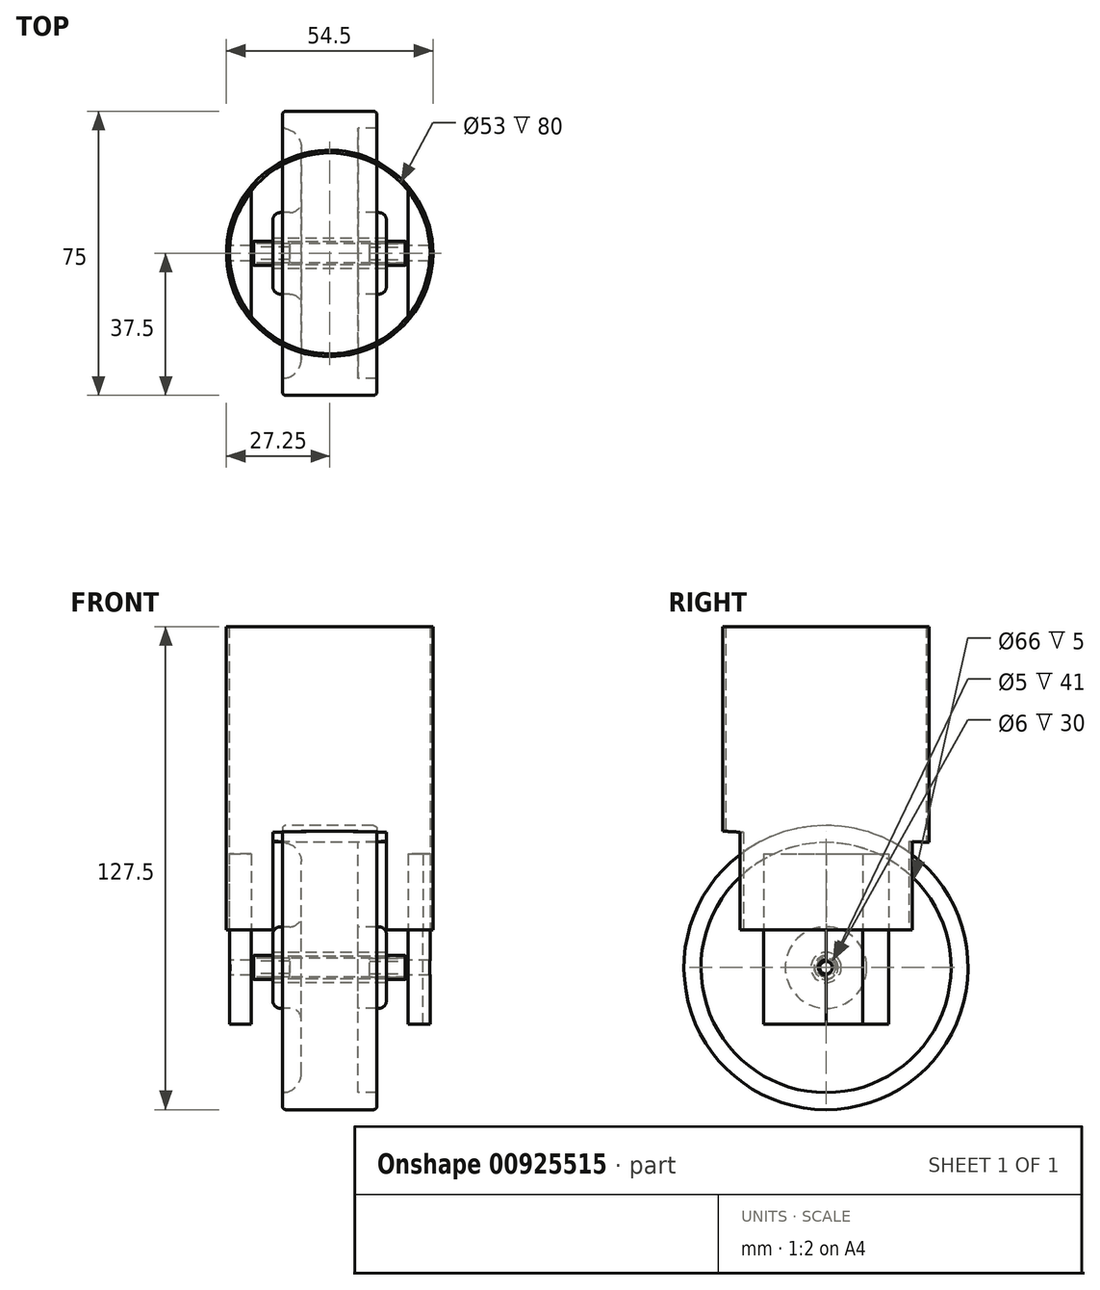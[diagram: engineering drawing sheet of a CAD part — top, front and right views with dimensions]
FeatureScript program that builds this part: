
annotation { "Feature Type Name" : "Feature", "Feature Type Description" : "" }
export const myFeature = defineFeature(function(context is Context, id is Id, definition is map)
    precondition{}
    {
        {
            var Q0;
            Q0=qCreatedBy(makeId("Right.planeOp"),FACE);
            var sketch = newSketch(context, id + "F0", { "sketchPlane" : qUnion([Q0])});
            skCircle(sketch, "E0", {"center": v(0, 0) * mm, "radius": 4 * mm});
            skCircle(sketch, "E1", {"center": v(0, 0) * mm, "radius": 10.75 * mm});
            skCircle(sketch, "E2", {"center": v(0, 0) * mm, "radius": 37.5 * mm});
            skCircle(sketch, "E3", {"center": v(0, 0) * mm, "radius": 33 * mm});
            skSolve(sketch);
        }
        {
            var Q0;
            Q0=makeQuery(id+"F0.imprint","IMPRINT",FACE,{"disambiguationData":[TD([[makeQuery(id+"F0.imprint","IMPRINT",EDGE,{"derivedFrom":sQuery(id+"F0.wireOp",EDGE,"E2")}),1.0]])]});
            extrude(context, id + "F1", {"entities" : qUnion([Q0]), "endBound" : BoundingType.SYMMETRIC, "depth" : 25 * mm, "offsetDistance" : 25 * mm});
        }
        {
            var Q0;
            Q0=makeQuery(id+"F0.imprint","IMPRINT",FACE,{"disambiguationData":[TD([[makeQuery(id+"F0.imprint","IMPRINT",EDGE,{"derivedFrom":sQuery(id+"F0.wireOp",EDGE,"E1")}),-1.0]])]});
            extrude(context, id + "F2", {"entities" : qUnion([Q0]), "operationType" : NewBodyOperationType.ADD, "endBound" : BoundingType.SYMMETRIC, "depth" : 15 * mm, "offsetDistance" : 25 * mm});
        }
        {
            var Q0;
            Q0=makeQuery(id+"F0.imprint","IMPRINT",FACE,{"disambiguationData":[TD([[makeQuery(id+"F0.imprint","IMPRINT",EDGE,{"derivedFrom":sQuery(id+"F0.wireOp",EDGE,"E0")}),-1.0]])]});
            extrude(context, id + "F3", {"entities" : qUnion([Q0]), "operationType" : NewBodyOperationType.ADD, "endBound" : BoundingType.SYMMETRIC, "depth" : 30 * mm, "offsetDistance" : 25 * mm});
        }
        {
            var Q0;
            Q0=makeQuery(id+"F2.opExtrude","CAP_EDGE",EDGE,{"disambiguationData":[OSD([sQuery(id+"F0.wireOp",EDGE,"E3")])],"isStart":false});
            var Q1;
            Q1=makeQuery(id+"F2.opExtrude","CAP_EDGE",EDGE,{"disambiguationData":[OSD([sQuery(id+"F0.wireOp",EDGE,"E3")])],"isStart":true});
            fillet(context, id + "F4", {"entities" : qUnion([Q0, Q1]), "radius" : 5 * mm, "tangentPropagation" : true, "allowEdgeOverflow" : false});
        }
        {
            var Q0;
            Q0=makeQuery(id+"F2.opExtrude","CAP_EDGE",EDGE,{"disambiguationData":[OSD([sQuery(id+"F0.wireOp",EDGE,"E1")])],"isStart":true});
            var Q1;
            Q1=makeQuery(id+"F2.opExtrude","CAP_EDGE",EDGE,{"disambiguationData":[OSD([sQuery(id+"F0.wireOp",EDGE,"E1")])],"isStart":false});
            fillet(context, id + "F5", {"entities" : qUnion([Q0, Q1]), "radius" : 3 * mm, "tangentPropagation" : true, "allowEdgeOverflow" : false});
        }
        {
            var Q0;
            Q0=makeQuery(id+"F3.opExtrude","CAP_EDGE",EDGE,{"disambiguationData":[OSD([sQuery(id+"F0.wireOp",EDGE,"E1")])],"isStart":false});
            var Q1;
            Q1=makeQuery(id+"F3.opExtrude","CAP_EDGE",EDGE,{"disambiguationData":[OSD([sQuery(id+"F0.wireOp",EDGE,"E1")])],"isStart":true});
            fillet(context, id + "F6", {"entities" : qUnion([Q0, Q1]), "radius" : 2 * mm, "tangentPropagation" : true, "allowEdgeOverflow" : false});
        }
        {
            var Q0;
            Q0=makeQuery(id+"F1.opExtrude","CAP_EDGE",EDGE,{"disambiguationData":[OSD([sQuery(id+"F0.wireOp",EDGE,"E2")])],"isStart":true});
            var Q1;
            {var subQ0=sQuery(id+"F0.wireOp",EDGE,"E3");Q1=makeQuery(id+"F4.opFillet","BLEND_EDGE",EDGE,{"blendedFrom":[makeQuery(id+"F2.opExtrude","CAP_EDGE",EDGE,{"disambiguationData":[OSD([subQ0])],"isStart":true}),makeQuery(id+"F1.opExtrude","CAP_FACE",FACE,{"disambiguationData":[OSD([sQuery(id+"F0.wireOp",EDGE,"E2"),subQ0])],"isStart":true})],"blendedInto":[makeQuery(id+"F1.opExtrude","CAP_FACE",FACE,{"disambiguationData":[OSD([sQuery(id+"F0.wireOp",EDGE,"E2"),subQ0])],"isStart":true})]});}
            var Q2;
            Q2=makeQuery(id+"F1.opExtrude","CAP_EDGE",EDGE,{"disambiguationData":[OSD([sQuery(id+"F0.wireOp",EDGE,"E2")])],"isStart":false});
            var Q3;
            {var subQ0=sQuery(id+"F0.wireOp",EDGE,"E3");Q3=makeQuery(id+"F4.opFillet","BLEND_EDGE",EDGE,{"blendedFrom":[makeQuery(id+"F2.opExtrude","CAP_EDGE",EDGE,{"disambiguationData":[OSD([subQ0])],"isStart":false}),makeQuery(id+"F1.opExtrude","CAP_FACE",FACE,{"disambiguationData":[OSD([sQuery(id+"F0.wireOp",EDGE,"E2"),subQ0])],"isStart":false})],"blendedInto":[makeQuery(id+"F1.opExtrude","CAP_FACE",FACE,{"disambiguationData":[OSD([sQuery(id+"F0.wireOp",EDGE,"E2"),subQ0])],"isStart":false})]});}
            fillet(context, id + "F7", {"entities" : qUnion([Q0, Q1, Q2, Q3]), "radius" : 1 * mm, "tangentPropagation" : true, "allowEdgeOverflow" : false});
        }
        {
            var Q0;
            Q0=qCreatedBy(makeId("Right.planeOp"),FACE);
            var sketch = newSketch(context, id + "F8", { "sketchPlane" : qUnion([Q0])});
            skCircle(sketch, "E4", {"center": v(0, 0) * mm, "radius": 4 * mm});
            skCircle(sketch, "E5", {"center": v(0, 0) * mm, "radius": 3 * mm});
            skSolve(sketch);
        }
        {
            var Q0;
            Q0=makeQuery(id+"F8.imprint","IMPRINT",FACE,{"disambiguationData":[TD([[makeQuery(id+"F8.imprint","IMPRINT",EDGE,{"derivedFrom":sQuery(id+"F8.wireOp",EDGE,"E4")}),1.0]])]});
            extrude(context, id + "F9", {"entities" : qUnion([Q0]), "endBound" : BoundingType.SYMMETRIC, "depth" : 30 * mm, "offsetDistance" : 25 * mm});
        }
        {
            var Q0;
            Q0=qCreatedBy(makeId("Right.planeOp"),FACE);
            var sketch = newSketch(context, id + "F10", { "sketchPlane" : qUnion([Q0])});
            skCircle(sketch, "E6", {"center": v(0, 0) * mm, "radius": 3 * mm});
            skCircle(sketch, "E7", {"center": v(0, 0) * mm, "radius": 2.5 * mm});
            skSolve(sketch);
        }
        {
            var Q0;
            Q0=makeQuery(id+"F10.imprint","IMPRINT",FACE,{"disambiguationData":[TD([[makeQuery(id+"F10.imprint","IMPRINT",EDGE,{"derivedFrom":sQuery(id+"F10.wireOp",EDGE,"E6")}),1.0]])]});
            extrude(context, id + "F11", {"entities" : qUnion([Q0]), "endBound" : BoundingType.SYMMETRIC, "depth" : 41 * mm, "offsetDistance" : 25 * mm});
        }
        {
            var Q0;
            Q0=makeQuery(id+"F11.opExtrude","CAP_FACE",FACE,{"disambiguationData":[OSD([sQuery(id+"F10.wireOp",EDGE,"E6"),sQuery(id+"F10.wireOp",EDGE,"E7")])],"isStart":false});
            var sketch = newSketch(context, id + "F12", { "sketchPlane" : qUnion([Q0])});
            skCircle(sketch, "E8", {"center": v(0, 0) * mm, "radius": 2.5 * mm});
            skCircle(sketch, "E9", {"center": v(0, 0) * mm, "radius": 1.65 * mm});
            skSolve(sketch);
        }
        {
            var Q0;
            Q0=makeQuery(id+"F12.imprint","IMPRINT",FACE,{"disambiguationData":[TD([[makeQuery(id+"F12.imprint","IMPRINT",EDGE,{"derivedFrom":sQuery(id+"F12.wireOp",EDGE,"E8")}),1.0]])]});
            extrude(context, id + "F13", {"entities" : qUnion([Q0]), "oppositeDirection" : true, "depth" : 10 * mm, "offsetDistance" : 25 * mm});
        }
        {
            var Q0;
            Q0=makeQuery(id+"F11.opExtrude","CAP_FACE",FACE,{"disambiguationData":[OSD([sQuery(id+"F10.wireOp",EDGE,"E6"),sQuery(id+"F10.wireOp",EDGE,"E7")])],"isStart":true});
            var sketch = newSketch(context, id + "F14", { "sketchPlane" : qUnion([Q0])});
            skCircle(sketch, "E10", {"center": v(0, 0) * mm, "radius": 2.5 * mm});
            skCircle(sketch, "E11", {"center": v(0, 0) * mm, "radius": 1.65 * mm});
            skSolve(sketch);
        }
        {
            var Q0;
            Q0=makeQuery(id+"F14.imprint","IMPRINT",FACE,{"disambiguationData":[TD([[makeQuery(id+"F14.imprint","IMPRINT",EDGE,{"derivedFrom":sQuery(id+"F14.wireOp",EDGE,"E10")}),-1.0]])]});
            extrude(context, id + "F15", {"entities" : qUnion([Q0]), "oppositeDirection" : true, "depth" : 10 * mm, "offsetDistance" : 25 * mm});
        }
        {
            var Q0;
            Q0=makeQuery(id+"F9.opExtrude","CAP_FACE",FACE,{"disambiguationData":[OSD([sQuery(id+"F8.wireOp",EDGE,"E4"),sQuery(id+"F8.wireOp",EDGE,"E5")])],"isStart":false});
            var sketch = newSketch(context, id + "F16", { "sketchPlane" : qUnion([Q0])});
            skCircle(sketch, "E12", {"center": v(0, 0) * mm, "radius": 3.03 * mm});
            skCircle(sketch, "E13", {"center": v(0, 0) * mm, "radius": 3.18 * mm});
            skSolve(sketch);
        }
        {
            var Q0;
            Q0=makeQuery(id+"F16.imprint","IMPRINT",FACE,{"disambiguationData":[TD([[makeQuery(id+"F16.imprint","IMPRINT",EDGE,{"derivedFrom":sQuery(id+"F16.wireOp",EDGE,"E12")}),-1.0]])]});
            extrude(context, id + "F17", {"entities" : qUnion([Q0]), "depth" : 5 * mm, "offsetDistance" : 25 * mm});
        }
        {
            var Q0;
            Q0=makeQuery(id+"F9.opExtrude","CAP_FACE",FACE,{"disambiguationData":[OSD([sQuery(id+"F8.wireOp",EDGE,"E4"),sQuery(id+"F8.wireOp",EDGE,"E5")])],"isStart":true});
            var sketch = newSketch(context, id + "F18", { "sketchPlane" : qUnion([Q0])});
            skCircle(sketch, "E14", {"center": v(0, 0) * mm, "radius": 3.03 * mm});
            skCircle(sketch, "E15", {"center": v(0, 0) * mm, "radius": 3.18 * mm});
            skSolve(sketch);
        }
        {
            var Q0;
            Q0=makeQuery(id+"F18.imprint","IMPRINT",FACE,{"disambiguationData":[TD([[makeQuery(id+"F18.imprint","IMPRINT",EDGE,{"derivedFrom":sQuery(id+"F18.wireOp",EDGE,"E14")}),-1.0]])]});
            extrude(context, id + "F19", {"entities" : qUnion([Q0]), "depth" : 5 * mm, "offsetDistance" : 25 * mm});
        }
        {
            var Q0;
            Q0=qCreatedBy(makeId("Top.planeOp"),FACE);
            cPlane(context, id + "F20", {"entities" : qUnion([Q0]), "cplaneType" : CPlaneType.OFFSET, "offset" : 10 * mm, "width" : 150 * mm, "height" : 150 * mm});
        }
        {
            var Q0;
            Q0=qCreatedBy(id+"F20.planeOp",FACE);
            var sketch = newSketch(context, id + "F21", { "sketchPlane" : qUnion([Q0])});
            skCircle(sketch, "E16", {"center": v(0, 0) * mm, "radius": 27.25 * mm});
            skCircle(sketch, "E17", {"center": v(0, 0) * mm, "radius": 26.5 * mm});
            skSolve(sketch);
        }
        {
            var Q0;
            Q0=makeQuery(id+"F21.imprint","IMPRINT",FACE,{"disambiguationData":[TD([[makeQuery(id+"F21.imprint","IMPRINT",EDGE,{"derivedFrom":sQuery(id+"F21.wireOp",EDGE,"E16")}),1.0]])]});
            extrude(context, id + "F22", {"entities" : qUnion([Q0]), "depth" : 80 * mm, "offsetDistance" : 25 * mm});
        }
        {
            var Q0;
            Q0=qCreatedBy(makeId("Right.planeOp"),FACE);
            var sketch = newSketch(context, id + "F23", { "sketchPlane" : qUnion([Q0])});
            skPoint(sketch, "E18", {"position": v(-27.28, 36) * mm});
            skPoint(sketch, "E19", {"position": v(27.39, 33) * mm});
            skLineSegment(sketch, "E20", {"start": v(-27.28, 36) * mm, "end": v(27.39, 33) * mm});
            skLineSegment(sketch, "E21", {"start": v(-27.28, 36) * mm, "end": v(-27.28, 8.2) * mm});
            skLineSegment(sketch, "E22", {"start": v(27.39, 33) * mm, "end": v(27.39, 8.06) * mm});
            skLineSegment(sketch, "E23", {"start": v(27.39, 8.06) * mm, "end": v(-27.28, 8.2) * mm});
            skSolve(sketch);
        }
        {
            var Q0;
            Q0=makeQuery(id+"F23.imprint","IMPRINT",FACE,{"disambiguationData":[TD([[makeQuery(id+"F23.imprint","IMPRINT",EDGE,{"derivedFrom":sQuery(id+"F23.wireOp",EDGE,"E20")}),-1.0]])]});
            extrude(context, id + "F24", {"entities" : qUnion([Q0]), "endBound" : BoundingType.SYMMETRIC, "depth" : 30 * mm, "offsetDistance" : 25 * mm});
        }
        {
            var Q0;
            Q0=makeQuery(id+"F24.opExtrude","SWEPT_BODY",BODY,{"disambiguationData":[OSD([sQuery(id+"F23.wireOp",EDGE,"E20"),sQuery(id+"F23.wireOp",EDGE,"E21"),sQuery(id+"F23.wireOp",EDGE,"E22"),sQuery(id+"F23.wireOp",EDGE,"E23")])]});
            var Q1;
            Q1=makeQuery(id+"F22.opExtrude","SWEPT_BODY",BODY,{"disambiguationData":[OSD([sQuery(id+"F21.wireOp",EDGE,"E16"),sQuery(id+"F21.wireOp",EDGE,"E17")])]});
            booleanBodies(context, id + "F25", {"operationType" : BooleanOperationType.SUBTRACTION, "tools" : qUnion([Q0]), "targets" : qUnion([Q1])});
        }
        {
            var Q0;
            {var subQ0=sQuery(id+"F21.wireOp",EDGE,"E16");var subQ1=sQuery(id+"F21.wireOp",EDGE,"E17");Q0=makeQuery(id+"F25.opBoolean","SPLIT",FACE,{"disambiguationData":[TD([makeQuery(id+"F24.opExtrude","CAP_FACE",FACE,{"disambiguationData":[OSD([sQuery(id+"F23.wireOp",EDGE,"E20"),sQuery(id+"F23.wireOp",EDGE,"E21"),sQuery(id+"F23.wireOp",EDGE,"E22"),sQuery(id+"F23.wireOp",EDGE,"E23")])],"isStart":false})])],"derivedFrom":makeQuery(id+"F22.opExtrude","CAP_FACE",FACE,{"disambiguationData":[OSD([subQ0,subQ1])],"isStart":true})});}
            var sketch = newSketch(context, id + "F26", { "sketchPlane" : qUnion([Q0])});
            skPoint(sketch, "E24", {"position": v(20.71, 16.5) * mm});
            skLineSegment(sketch, "E25", {"start": v(20.71, 16.5) * mm, "end": v(20.71, -16.53) * mm});
            skFitSpline(sketch, "E26", {"points": [v(20.71, 16.5) * mm, v(24.26, 10.65) * mm, v(26.5, 0) * mm, v(24.67, -9.68) * mm, v(20.71, -16.53) * mm], "startDerivative": vector(17.06, -23.83) * mm, "endDerivative": vector(-18.16, -27.31) * mm});
            skLineSegment(sketch, "E27", {"start": v(0.03, -15.49) * mm, "end": v(0, -238.8) * mm, "construction": true});
            skLineSegment(sketch, "E28.MirrorCS", {"start": v(-20.64, 16.51) * mm, "end": v(-20.65, -16.52) * mm});
            skFitSpline(sketch, "E29.MirrorCS", {"points": [v(-20.64, 16.51) * mm, v(-24.2, 10.66) * mm, v(-26.43, 0) * mm, v(-24.6, -9.68) * mm, v(-20.65, -16.52) * mm], "startDerivative": vector(-17.06, -23.83) * mm, "endDerivative": vector(18.15, -27.32) * mm});
            skSolve(sketch);
        }
        {
            var Q0;
            {var subQ6=sQuery(id+"F26.wireOp",EDGE,"E25");Q0=makeQuery(id+"F26.imprint","IMPRINT",FACE,{"disambiguationData":[TD([[makeQuery(id+"F26.imprint","IMPRINT",EDGE,{"derivedFrom":subQ6}),1.0]])]});}
            var Q1;
            Q1=makeQuery(id+"F26.imprint","IMPRINT",FACE,{"disambiguationData":[TD([[makeQuery(id+"F26.imprint","IMPRINT",EDGE,{"derivedFrom":sQuery(id+"F26.wireOp",EDGE,"E28.MirrorCS")}),-1.0]])]});
            extrude(context, id + "F27", {"entities" : qUnion([Q0, Q1]), "depth" : 25 * mm, "offsetDistance" : 25 * mm});
        }
        {
            var Q0;
            Q0=makeQuery(id+"F26.imprint","IMPRINT",FACE,{"disambiguationData":[TD([[makeQuery(id+"F26.imprint","IMPRINT",EDGE,{"derivedFrom":sQuery(id+"F26.wireOp",EDGE,"E28.MirrorCS")}),-1.0]])]});
            var Q1;
            {var subQ6=sQuery(id+"F26.wireOp",EDGE,"E25");Q1=makeQuery(id+"F26.imprint","IMPRINT",FACE,{"disambiguationData":[TD([[makeQuery(id+"F26.imprint","IMPRINT",EDGE,{"derivedFrom":subQ6}),1.0]])]});}
            extrude(context, id + "F28", {"entities" : qUnion([Q0, Q1]), "oppositeDirection" : true, "depth" : 20 * mm, "offsetDistance" : 25 * mm});
        }
        {
            var Q0;
            Q0=qCreatedBy(makeId("Right.planeOp"),FACE);
            var sketch = newSketch(context, id + "F29", { "sketchPlane" : qUnion([Q0])});
            skCircle(sketch, "E30", {"center": v(0, 0) * mm, "radius": 2 * mm});
            skSolve(sketch);
        }
        {
            var Q0;
            Q0 = qSketchRegion(id + "F29", true);
            extrude(context, id + "F30", {"entities" : qUnion([Q0]), "endBound" : BoundingType.SYMMETRIC, "depth" : 100 * mm, "offsetDistance" : 25 * mm});
        }
        {
            var Q0;
            Q0=makeQuery(id+"F30.opExtrude","SWEPT_BODY",BODY,{"disambiguationData":[OSD([sQuery(id+"F29.wireOp",EDGE,"E30")])]});
            var Q1;
            Q1=makeQuery(id+"F27.opExtrude","SWEPT_BODY",BODY,{"disambiguationData":[OSD([sQuery(id+"F26.wireOp",EDGE,"E28.MirrorCS"),sQuery(id+"F26.wireOp",EDGE,"E29.MirrorCS")])]});
            var Q2;
            Q2=makeQuery(id+"F27.opExtrude","SWEPT_BODY",BODY,{"disambiguationData":[OSD([sQuery(id+"F21.wireOp",EDGE,"E17"),sQuery(id+"F26.wireOp",EDGE,"E25"),sQuery(id+"F26.wireOp",EDGE,"E26")])]});
            booleanBodies(context, id + "F31", {"operationType" : BooleanOperationType.SUBTRACTION, "tools" : qUnion([Q0]), "targets" : qUnion([Q1, Q2])});
        }
    });
